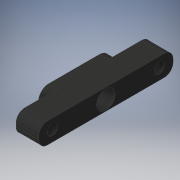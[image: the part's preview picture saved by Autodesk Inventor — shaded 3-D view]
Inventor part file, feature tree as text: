
AUTODESK INVENTOR PART (.ipt)
format: ipt  version: 2018 (Build 220112000, 112)  size: 143,360 bytes
history: native  units: in
note: dims shown in document units (in); Inventor stores cm internally (conversion verified against a paired STEP export)
features: extrude x6, sketch x6
ambient origin geometry x8: Origin, YZ Plane, XZ Plane, XY Plane, X Axis, Y Axis, Z Axis, Center Point
bodies: Solid1 (feature_tree), Solid2 (feature_tree)
feature tree (12):
  extrude  "Extrusion1"  Depth=1.16in
  extrude  "Extrusion2"  Depth=0.075in
  extrude  "Extrusion3"  Depth=0.1969in TaperAngle=0.0deg
  extrude  "Extrusion4"  Depth=0.0787in TaperAngle=0.0deg
  extrude  "Extrusion5"  Depth=0.0787in TaperAngle=0.0deg
  extrude  "Extrusion6"  [1 undecoded]
  sketch  "Sketch1"  dims[d0=0.18in d1=1.16in]
  sketch  "Sketch2"  dims[d2=0.075in d3=0.121in]
  sketch  "Sketch3"  dims[d4=0.1969in d5=0.0in d6=0.0394in d7=0.0in]
  sketch  "Sketch4"  dims[d8=0.0787in d9=0.0in d10=0.0787in d11=0.0in]
  sketch  "Sketch5"  dims[d12=0.0787in d13=0.0in d14=0.0787in d15=0.0in]
  sketch  "Sketch6"
note: 1 required parameter value undecoded (feature->parameter linkage not recoverable at this tier; creation-order binding heuristic only, values carry confidence <= 0.55)
